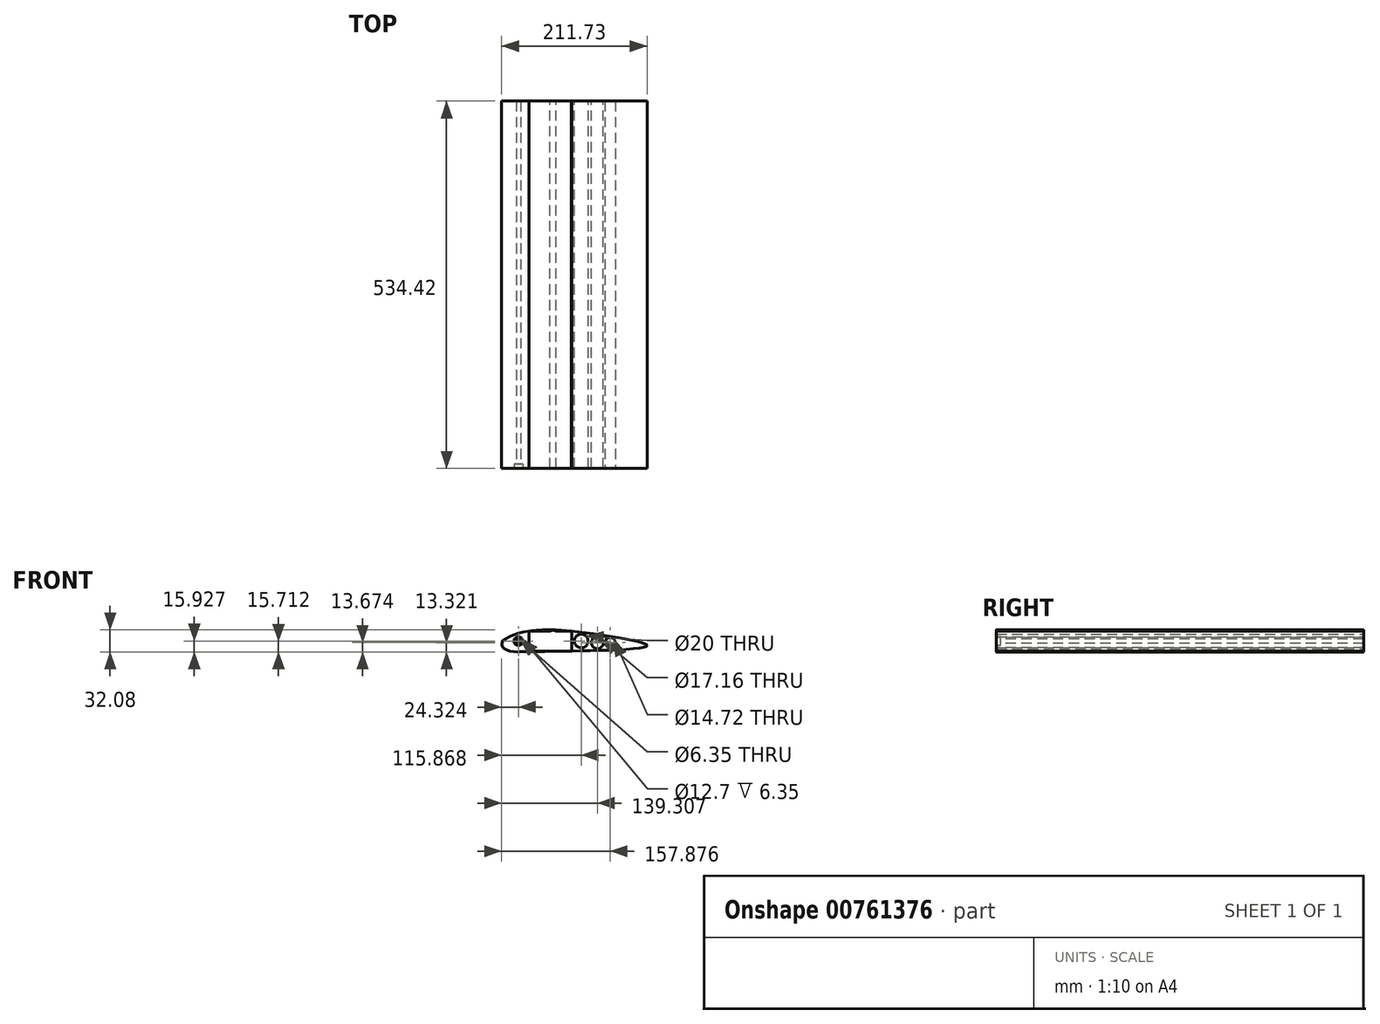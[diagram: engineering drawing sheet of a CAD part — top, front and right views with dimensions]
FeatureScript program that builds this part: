
annotation { "Feature Type Name" : "Feature", "Feature Type Description" : "" }
export const myFeature = defineFeature(function(context is Context, id is Id, definition is map)
    precondition{}
    {
        {
            var Q0;
            Q0=qCreatedBy(makeId("Front.planeOp"),FACE);
            var sketch = newSketch(context, id + "F0", { "sketchPlane" : qUnion([Q0])});
            skFitSpline(sketch, "E0", {"points": [v(173.39, 13.89) * mm, v(29.46, 6.35) * mm, v(21.9, 6.05) * mm, v(-9.36, 6.1) * mm, v(-16.92, 5.56) * mm, v(-29.27, 7.7) * mm, v(-35.06, 11.09) * mm, v(-37.3, 14.13) * mm, v(-37.14, 20.11) * mm, v(-30.84, 25.4) * mm, v(-15.85, 32.07) * mm, v(13.68, 36.92) * mm, v(74.98, 34.54) * mm, v(173.39, 13.89) * mm]});
            skSolve(sketch);
        }
        {
            var Q0;
            Q0=makeQuery(id+"F0.imprint","IMPRINT",FACE,{"disambiguationData":[TD([[makeQuery(id+"F0.imprint","IMPRINT",EDGE,{"derivedFrom":sQuery(id+"F0.wireOp",EDGE,"E0")}),-1.0]])]});
            extrude(context, id + "F1", {"entities" : qUnion([Q0]), "depth" : 534.42 * mm, "offsetDistance" : 25.4 * mm});
        }
        {
            var Q0;
            Q0=makeQuery(id+"F1.opExtrude","CAP_FACE",FACE,{"disambiguationData":[OSD([sQuery(id+"F0.wireOp",EDGE,"E0")])],"isStart":false});
            var sketch = newSketch(context, id + "F2", { "sketchPlane" : qUnion([Q0])});
            skCircle(sketch, "E1", {"center": v(-13.45, 21.27) * mm, "radius": 9.29 * mm});
            skSolve(sketch);
        }
        {
            var Q0;
            Q0=sQuery(id+"F2.wireOp",VERTEX,"E1.center");
            var Q1;
            Q1=makeQuery(id+"F1.opExtrude","SWEPT_BODY",BODY,{"disambiguationData":[OSD([sQuery(id+"F0.wireOp",EDGE,"E0")])]});
            hole(context, id + "F3", {"style" : HoleStyle.C_BORE, "endStyle" : HoleEndStyle.THROUGH, "holeDiameter" : 6.35 * mm, "cBoreDiameter" : 12.7 * mm, "cBoreDepth" : 6.35 * mm, "majorDiameter" : 6.35 * mm, "isTappedThrough" : true, "tappedDepth" : 12.7 * mm, "tapClearance" : 3, "locations" : qUnion([Q0]), "scope" : qUnion([Q1])});
        }
        {
            var Q0;
            Q0=makeQuery(id+"F1.opExtrude","CAP_FACE",FACE,{"disambiguationData":[OSD([sQuery(id+"F0.wireOp",EDGE,"E0")])],"isStart":true});
            var sketch = newSketch(context, id + "F4", { "sketchPlane" : qUnion([Q0])});
            skCircle(sketch, "E2", {"center": v(-36.89, 28.14) * mm, "radius": 8.75 * mm});
            skSolve(sketch);
        }
        {
            var Q0;
            Q0=makeQuery(id+"F4.imprint","IMPRINT",FACE,{"disambiguationData":[TD([[makeQuery(id+"F4.imprint","IMPRINT",EDGE,{"derivedFrom":sQuery(id+"F4.wireOp",EDGE,"E2")}),1.0]])]});
            extrude(context, id + "F5", {"entities" : qUnion([Q0]), "operationType" : NewBodyOperationType.REMOVE, "oppositeDirection" : true, "depth" : 703.33 * mm, "offsetDistance" : 25.4 * mm});
        }
        {
            var Q0;
            Q0=makeQuery(id+"F1.opExtrude","CAP_FACE",FACE,{"disambiguationData":[OSD([sQuery(id+"F0.wireOp",EDGE,"E0")])],"isStart":true});
            var sketch = newSketch(context, id + "F6", { "sketchPlane" : qUnion([Q0])});
            skCircle(sketch, "E3", {"center": v(-55.36, 22.6) * mm, "radius": 8.91 * mm});
            skCircle(sketch, "E4", {"center": v(-78.1, 21.49) * mm, "radius": 10 * mm});
            skCircle(sketch, "E5", {"center": v(-101.54, 18.88) * mm, "radius": 8.58 * mm});
            skSolve(sketch);
        }
        {
            var Q0;
            Q0 = qSketchRegion(id + "F6", true);
            extrude(context, id + "F7", {"entities" : qUnion([Q0]), "operationType" : NewBodyOperationType.REMOVE, "oppositeDirection" : true, "depth" : 728.98 * mm, "offsetDistance" : 25.4 * mm});
        }
        {
            var Q0;
            Q0=makeQuery(id+"F1.opExtrude","CAP_FACE",FACE,{"disambiguationData":[OSD([sQuery(id+"F0.wireOp",EDGE,"E0")])],"isStart":false});
            var sketch = newSketch(context, id + "F8", { "sketchPlane" : qUnion([Q0])});
            skLineSegment(sketch, "E6.bottom", {"start": v(2.3, 35.75) * mm, "end": v(64.54, 35.75) * mm});
            skLineSegment(sketch, "E6.top", {"start": v(2.3, 6.87) * mm, "end": v(64.54, 6.87) * mm});
            skLineSegment(sketch, "E6.left", {"start": v(2.3, 35.75) * mm, "end": v(2.3, 6.87) * mm});
            skLineSegment(sketch, "E6.right", {"start": v(64.54, 35.75) * mm, "end": v(64.54, 6.87) * mm});
            skSolve(sketch);
        }
        {
            var Q0;
            Q0 = qSketchRegion(id + "F8", true);
            extrude(context, id + "F9", {"entities" : qUnion([Q0]), "operationType" : NewBodyOperationType.REMOVE, "oppositeDirection" : true, "depth" : 623.57 * mm, "offsetDistance" : 25.4 * mm});
        }
        {
            var Q0;
            {var subQ0=sQuery(id+"F0.wireOp",EDGE,"E0");Q0=makeQuery(id+"F9.boolean.opBoolean","SPLIT",FACE,{"disambiguationData":[TD([makeQuery(id+"F7.boolean.opBoolean","COPY",FACE,{"derivedFrom":makeQuery(id+"F7.opExtrude","SWEPT_FACE",FACE,{"disambiguationData":[OSD([sQuery(id+"F6.wireOp",EDGE,"E4")])]})})])],"derivedFrom":makeQuery(id+"F1.opExtrude","CAP_FACE",FACE,{"disambiguationData":[OSD([subQ0])],"isStart":false})});}
            var sketch = newSketch(context, id + "F10", { "sketchPlane" : qUnion([Q0])});
            skCircle(sketch, "E7", {"center": v(120.1, 19.23) * mm, "radius": 7.36 * mm});
            skSolve(sketch);
        }
        {
            var Q0;
            Q0 = qSketchRegion(id + "F10", true);
            extrude(context, id + "F11", {"entities" : qUnion([Q0]), "operationType" : NewBodyOperationType.REMOVE, "oppositeDirection" : true, "depth" : 581.9 * mm, "offsetDistance" : 25.4 * mm});
        }
    });
